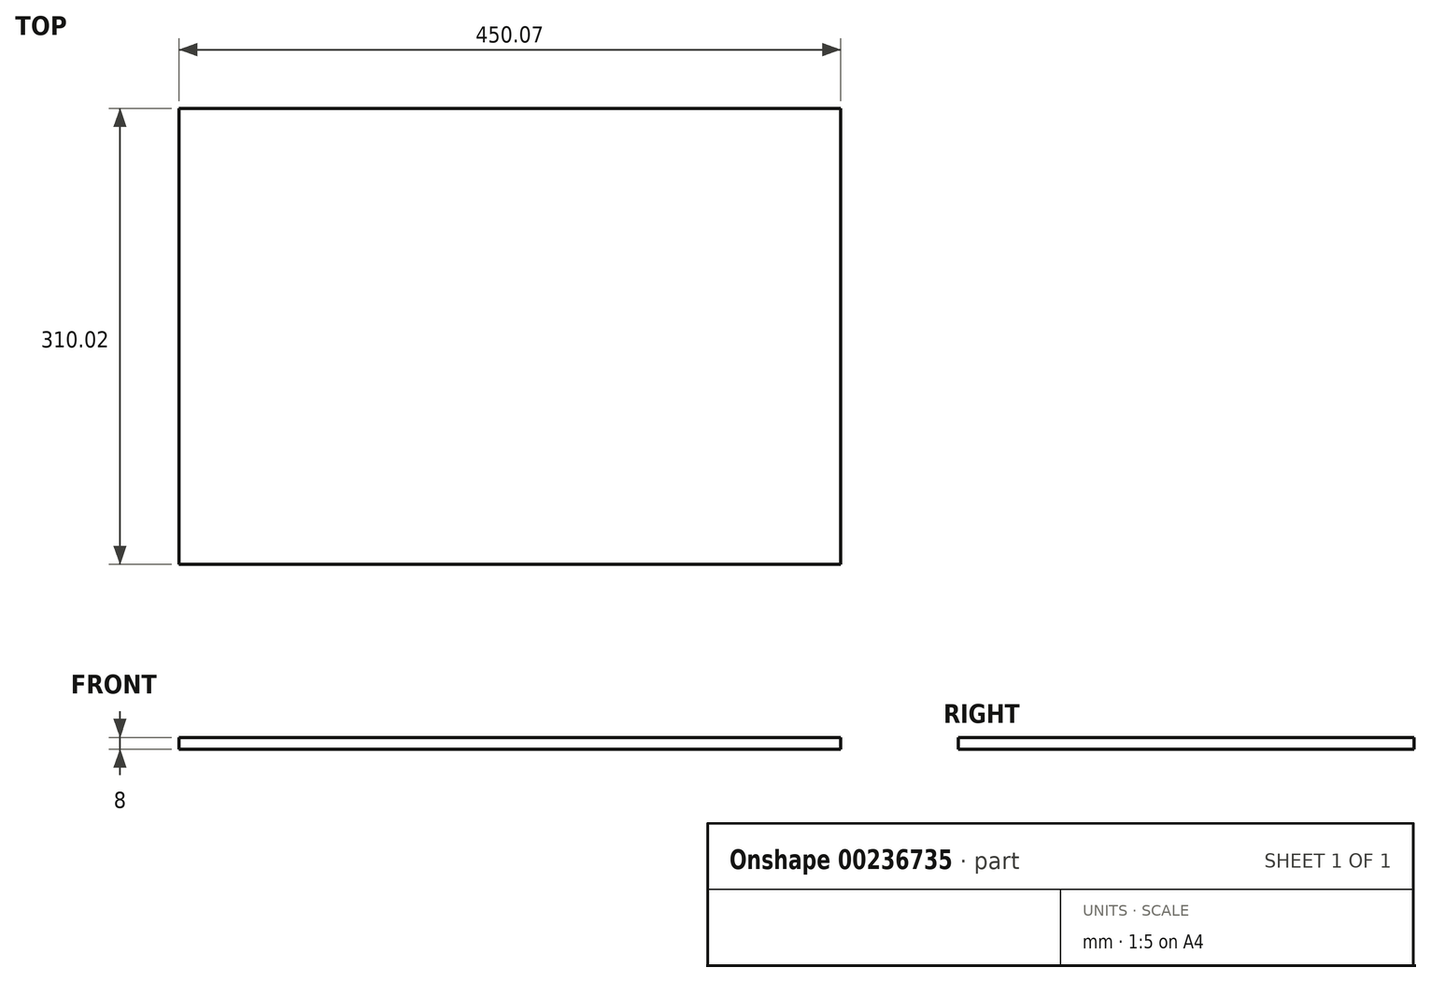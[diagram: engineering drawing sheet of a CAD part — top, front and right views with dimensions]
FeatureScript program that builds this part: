
annotation { "Feature Type Name" : "Feature", "Feature Type Description" : "" }
export const myFeature = defineFeature(function(context is Context, id is Id, definition is map)
    precondition{}
    {
        {
            var Q0;
            Q0=qCreatedBy(makeId("Top.planeOp"),FACE);
            var sketch = newSketch(context, id + "F0", { "sketchPlane" : qUnion([Q0])});
            skLineSegment(sketch, "E0.bottom", {"start": v(22.33, 174.47) * mm, "end": v(472.4, 174.47) * mm});
            skLineSegment(sketch, "E0.top", {"start": v(22.33, -135.55) * mm, "end": v(472.4, -135.55) * mm});
            skLineSegment(sketch, "E0.left", {"start": v(22.33, 174.47) * mm, "end": v(22.33, -135.55) * mm});
            skLineSegment(sketch, "E0.right", {"start": v(472.4, 174.47) * mm, "end": v(472.4, -135.55) * mm});
            skSolve(sketch);
        }
        {
            var Q0;
            Q0 = qSketchRegion(id + "F0", true);
            extrude(context, id + "F1", {"entities" : qUnion([Q0]), "depth" : 8 * mm, "offsetDistance" : 25 * mm});
        }
    });
